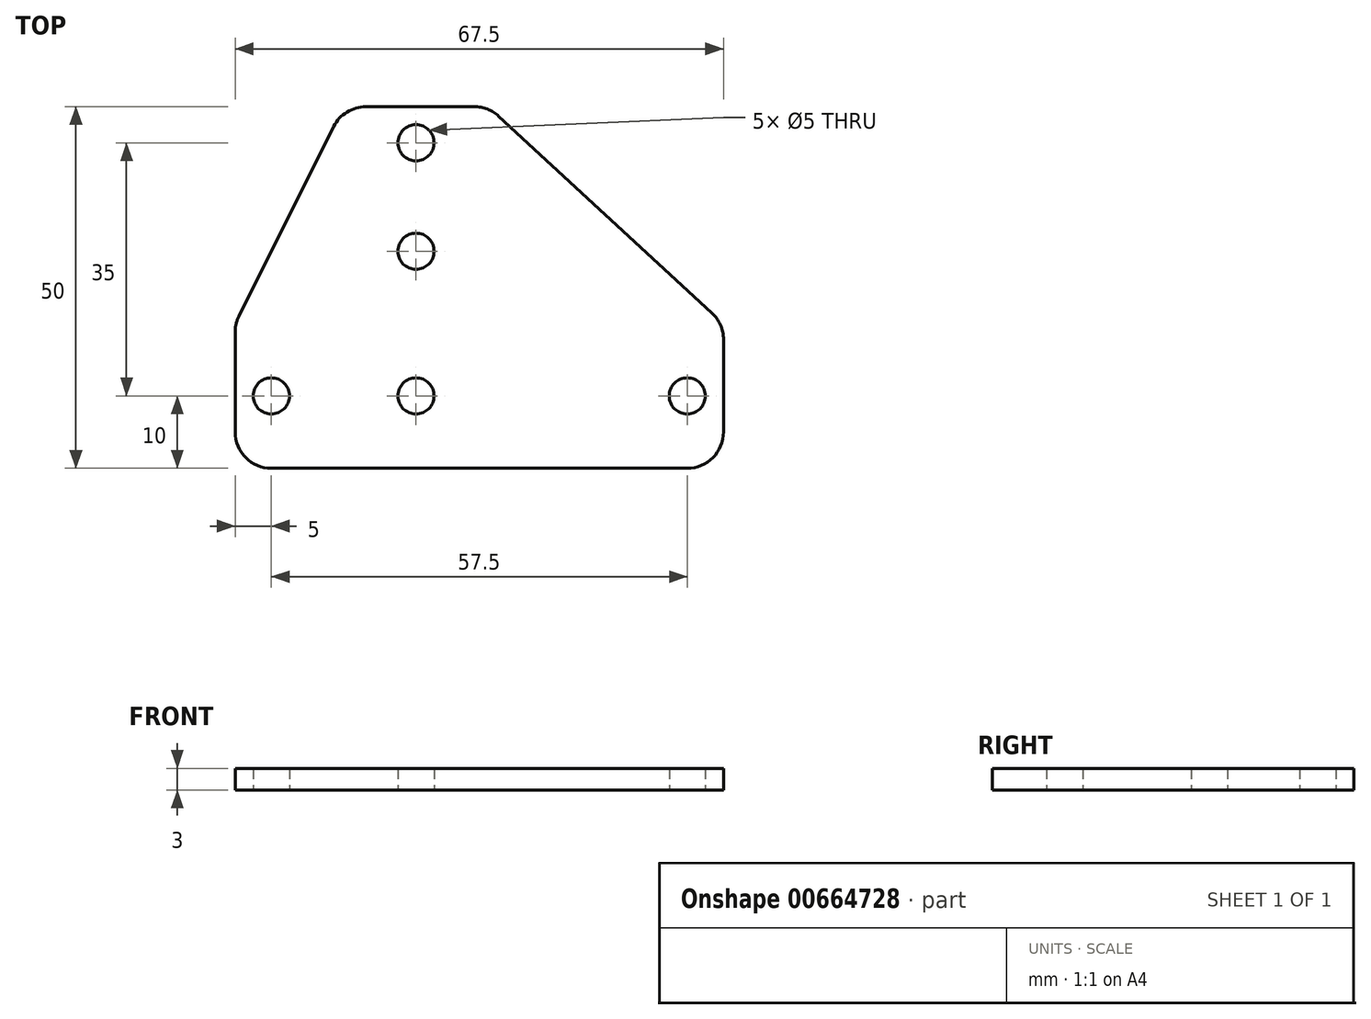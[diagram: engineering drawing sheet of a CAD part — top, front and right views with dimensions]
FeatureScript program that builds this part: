
annotation { "Feature Type Name" : "Feature", "Feature Type Description" : "" }
export const myFeature = defineFeature(function(context is Context, id is Id, definition is map)
    precondition{}
    {
        {
            var Q0;
            Q0=qCreatedBy(makeId("Top.planeOp"),FACE);
            var sketch = newSketch(context, id + "F0", { "sketchPlane" : qUnion([Q0])});
            skLineSegment(sketch, "E0", {"start": v(0, 5) * mm, "end": v(0, 18.82) * mm});
            skLineSegment(sketch, "E1", {"start": v(5, 0) * mm, "end": v(62.5, 0) * mm});
            skLineSegment(sketch, "E2.0", {"start": v(0, 10) * mm, "end": v(72.85, 10) * mm, "construction": true});
            skLineSegment(sketch, "E3.0", {"start": v(0, 20) * mm, "end": v(72.85, 20) * mm, "construction": true});
            skLineSegment(sketch, "E4.0", {"start": v(0, 30) * mm, "end": v(72.85, 30) * mm, "construction": true});
            skLineSegment(sketch, "E5.0", {"start": v(0, 45) * mm, "end": v(72.85, 45) * mm, "construction": true});
            skLineSegment(sketch, "E6.0", {"start": v(18.1, 50) * mm, "end": v(33.05, 50) * mm});
            skLineSegment(sketch, "E7.0", {"start": v(5, 0) * mm, "end": v(5, 53.67) * mm, "construction": true});
            skLineSegment(sketch, "E8.0", {"start": v(15, 0) * mm, "end": v(15, 53.67) * mm, "construction": true});
            skLineSegment(sketch, "E9.0", {"start": v(25, 0) * mm, "end": v(25, 53.67) * mm, "construction": true});
            skLineSegment(sketch, "E10.0", {"start": v(0, 25) * mm, "end": v(72.85, 25) * mm, "construction": true});
            skLineSegment(sketch, "E11.0", {"start": v(35, 0) * mm, "end": v(35, 53.67) * mm, "construction": true});
            skLineSegment(sketch, "E12.0", {"start": v(62.5, 0) * mm, "end": v(62.5, 53.67) * mm, "construction": true});
            skLineSegment(sketch, "E13.0", {"start": v(67.5, 5) * mm, "end": v(67.5, 17.81) * mm});
            skCircle(sketch, "E14", {"center": v(5, 10) * mm, "radius": 2.5 * mm});
            skCircle(sketch, "E15", {"center": v(62.5, 10) * mm, "radius": 2.5 * mm});
            skCircle(sketch, "E16", {"center": v(25, 10) * mm, "radius": 2.5 * mm});
            skCircle(sketch, "E17", {"center": v(25, 30) * mm, "radius": 2.5 * mm});
            skCircle(sketch, "E18", {"center": v(25, 45) * mm, "radius": 2.5 * mm});
            skLineSegment(sketch, "E19", {"start": v(0.53, 21.06) * mm, "end": v(13.62, 47.24) * mm});
            skLineSegment(sketch, "E20", {"start": v(36.44, 48.67) * mm, "end": v(65.9, 21.48) * mm});
            skArc(sketch, "E21.filletArc", {"start": v(18.1, 50) * mm, "mid": v(15.46, 49.25) * mm, "end": v(13.62, 47.24) * mm});
            skArc(sketch, "E22.filletArc", {"start": v(36.44, 48.67) * mm, "mid": v(34.87, 49.66) * mm, "end": v(33.05, 50) * mm});
            skArc(sketch, "E23.filletArc", {"start": v(67.5, 17.81) * mm, "mid": v(67.08, 19.82) * mm, "end": v(65.9, 21.48) * mm});
            skArc(sketch, "E24.filletArc", {"start": v(62.5, 0) * mm, "mid": v(66.04, 1.46) * mm, "end": v(67.5, 5) * mm});
            skPoint(sketch, "E25.visualSharp", {"position": v(0, 0) * mm});
            skArc(sketch, "E25.filletArc", {"start": v(0, 5) * mm, "mid": v(1.46, 1.46) * mm, "end": v(5, 0) * mm});
            skArc(sketch, "E26.filletArc", {"start": v(0.53, 21.06) * mm, "mid": v(0.13, 19.97) * mm, "end": v(0, 18.82) * mm});
            skSolve(sketch);
        }
        {
            var Q0;
            Q0=makeQuery(id+"F0.imprint","IMPRINT",FACE,{"disambiguationData":[TD([[makeQuery(id+"F0.imprint","IMPRINT",EDGE,{"derivedFrom":sQuery(id+"F0.wireOp",EDGE,"E14")}),-1.0]])]});
            extrude(context, id + "F1", {"entities" : qUnion([Q0]), "depth" : 3 * mm, "offsetDistance" : 25 * mm});
        }
    });
